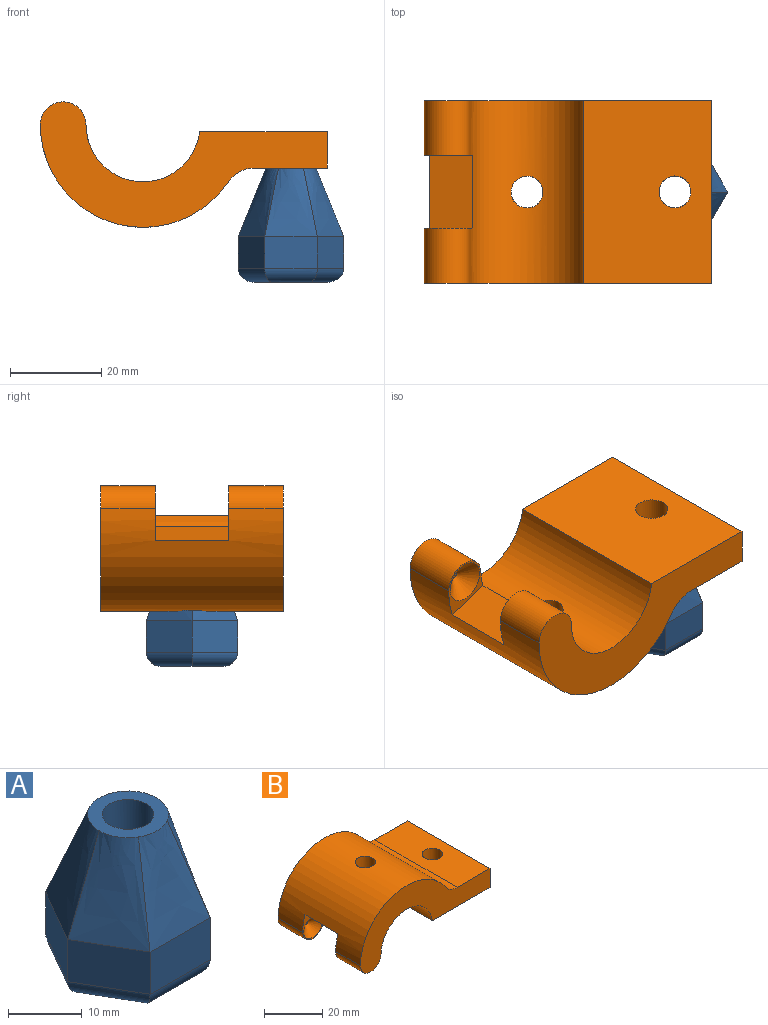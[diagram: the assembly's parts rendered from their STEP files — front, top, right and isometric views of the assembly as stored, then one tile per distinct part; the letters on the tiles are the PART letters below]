
ASSEMBLY  parts=2 mates=1
PART A: 28 faces, bbox 23.1x20x25 mm
  f0: plane 10x7mm, normal (0.87,0.5,0), area 80.8mm2, adj f1,f5,f13,f16
  f1: plane 11.55x7mm, normal (0,1,0), area 80.8mm2, adj f0,f2,f8,f14
  f2: plane 10x7mm, normal (-0.87,0.5,0), area 80.8mm2, adj f1,f3,f9,f15
  f3: plane 10x7mm, normal (-0.87,-0.5,0), area 80.8mm2, adj f2,f4,f10,f17
  f4: plane 11.55x7mm, normal (0,-1,0), area 80.8mm2, adj f3,f5,f11,f19
  f5: plane 10x7mm, normal (0.87,-0.5,0), area 80.8mm2, adj f0,f4,f12,f18
  f6: plane 16.17x14mm, normal (0,0,-1), area 45mm2, adj f14,f15,f16,f17,f18,f19,f20,f21
  f7: plane 11x11mm, normal (0,0,1), area 56.5mm2, adj f8,f9,f10,f11,f12,f13,f27
  f8: bspline ~15x11.55mm, area 135.6mm2, adj f1,f7,f9,f13
  f9: bspline ~15x10mm, area 135.6mm2, adj f2,f7,f8,f10
  f10: bspline ~15x10mm, area 135.6mm2, adj f3,f7,f9,f11
  f11: bspline ~15x11.55mm, area 135.6mm2, adj f4,f7,f10,f12
  f12: bspline ~15x10mm, area 135.6mm2, adj f5,f7,f11,f13
  f13: bspline ~15x10mm, area 135.6mm2, adj f0,f7,f8,f12
  f14: cylinder r=3mm len=11.55mm, axis (-1,0,0), area 48.5mm2, adj f1,f6,f15,f16
  f15: cylinder r=3mm len=11.5mm, axis (-0.5,-0.87,0), area 48.5mm2, adj f2,f6,f14,f17
  f16: cylinder r=3mm len=11.5mm, axis (-0.5,0.87,0), area 48.5mm2, adj f0,f6,f14,f18
  f17: cylinder r=3mm len=11.5mm, axis (0.5,-0.87,0), area 48.5mm2, adj f3,f6,f15,f19
  f18: cylinder r=3mm len=11.5mm, axis (0.5,0.87,0), area 48.5mm2, adj f5,f6,f16,f19
  f19: cylinder r=3mm len=11.55mm, axis (1,0,0), area 48.5mm2, adj f4,f6,f17,f18
  f20: plane 10x6.93mm, normal (0,1,0), area 69.3mm2, adj f6,f21,f25,f26
  f21: plane 10x6mm, normal (0.87,0.5,0), area 69.3mm2, adj f6,f20,f22,f26
  f22: plane 10x6mm, normal (0.87,-0.5,0), area 69.3mm2, adj f6,f21,f23,f26
  f23: plane 10x6.93mm, normal (0,-1,0), area 69.3mm2, adj f6,f22,f24,f26
  f24: plane 10x6mm, normal (-0.87,-0.5,0), area 69.3mm2, adj f6,f23,f25,f26
  f25: plane 10x6mm, normal (-0.87,0.5,0), area 69.3mm2, adj f6,f20,f24,f26
  f26: plane 13.86x12mm, normal (0,0,-1), area 86.2mm2, adj f20,f21,f22,f23,f24,f25,f27
  f27: cylinder r=3.5mm len=15mm, axis (0,0,-1), area 329.9mm2, adj f7,f26
PART B: 19 faces, bbox 62.9x40x27.5 mm
  f0: cylinder r=12.5mm len=40mm, axis (0,1,0), area 1408.9mm2, adj f4,f6,f7,f8,f9,f10,f11,f12
  f1: cylinder r=22.5mm len=41.15mm, axis (0,1,0), area 2141.5mm2, adj f5,f6,f7,f8,f9,f10,f11,f12
  f2: plane 40x8mm, normal (1,0,0), area 320mm2, adj f3,f4,f6,f9
  f3: plane 40x15.94mm, normal (0,0,1), area 599.2mm2, adj f2,f5,f6,f9,f17
  f4: plane 40x27.99mm, normal (0,0,-1), area 1081mm2, adj f0,f2,f6,f9,f17
  f5: cylinder r=7mm len=40mm, axis (0,1,0), area 273.6mm2, adj f1,f3,f6,f9
  f6: plane 62.9x27.5mm, normal (0,-1,0), area 726.2mm2, adj f0,f1,f2,f3,f4,f5,f7
  f7: cylinder r=5mm len=12mm, axis (0,-1,0), area 188.5mm2, adj f0,f1,f6,f8
  f8: plane 11.95x10.61mm, normal (0,1,0), area 28.6mm2, adj f0,f1,f7,f11,f13
  f9: plane 62.9x27.5mm, normal (0,1,0), area 726.2mm2, adj f0,f1,f2,f3,f4,f5,f10
  f10: cylinder r=5mm len=12mm, axis (0,1,0), area 188.5mm2, adj f0,f1,f9,f12
  f11: plane 16x9.51mm, normal (-0.31,0,-0.95), area 160mm2, adj f0,f1,f8,f12
  f12: plane 11.95x10.61mm, normal (0,-1,0), area 29.5mm2, adj f0,f1,f10,f11,f15
  f13: cone r=0.61mm half-angle=50deg, axis (0,1,0), area 84.2mm2, adj f8,f14
  f14: plane 1.22x1.22mm, normal (0,1,0), area 1.2mm2, adj f13
  f15: cone r=4.54mm half-angle=50deg, axis (0,-1,0), area 83mm2, adj f12,f16
  f16: plane 1.22x1.22mm, normal (0,-1,0), area 1.2mm2, adj f15
  f17: cylinder r=3.5mm len=8mm, axis (0,0,1), area 175.9mm2, adj f3,f4
  f18: cylinder r=3.5mm len=10.5mm, axis (0,0,-1), area 222.4mm2, adj f0,f1
PLACE A t=(35.03,28.88,0.47)mm
PLACE B rot(axis=(1,0,0),180deg) t=(2.61,8.88,34.97)mm
MATE cylindrical B.f17 <-> A.f27  axis (0,0,-1) through (35.03,28.88,25.47)mm
